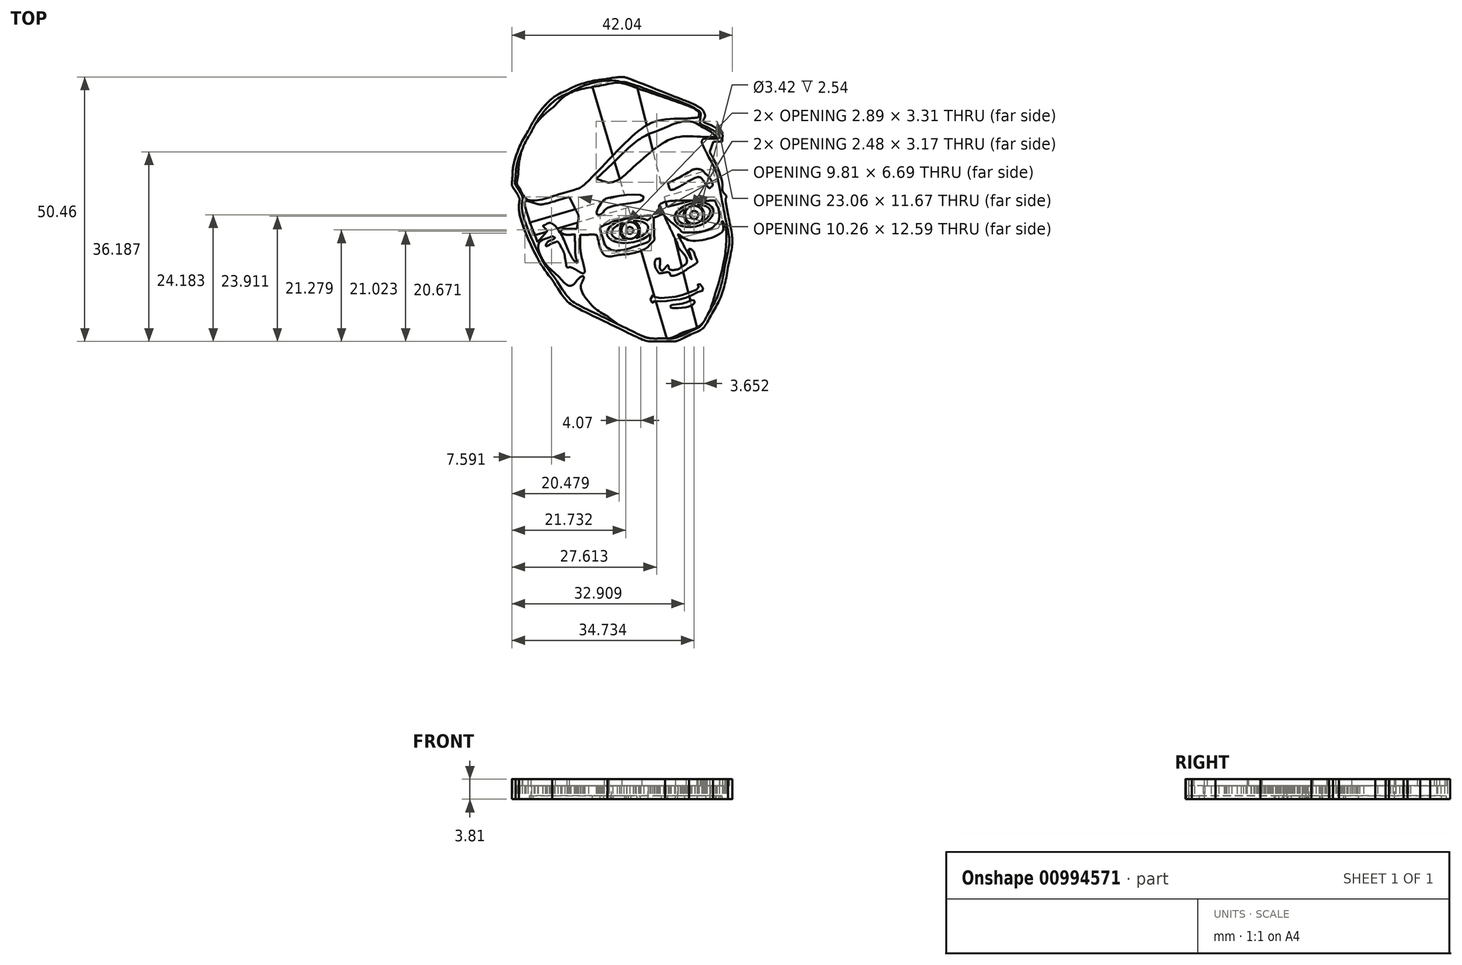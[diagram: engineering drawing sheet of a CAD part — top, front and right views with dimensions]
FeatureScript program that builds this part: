
annotation { "Feature Type Name" : "Feature", "Feature Type Description" : "" }
export const myFeature = defineFeature(function(context is Context, id is Id, definition is map)
    precondition{}
    {
        {
            var Q0;
            Q0=qCreatedBy(makeId("Top.planeOp"),FACE);
            var sketch = newSketch(context, id + "F0", { "sketchPlane" : qUnion([Q0])});
            skLineSegment(sketch, "E0", {"start": v(16.8, 11.07) * mm, "end": v(15.81, 13.05) * mm});
            skLineSegment(sketch, "E1", {"start": v(15.81, 13.05) * mm, "end": v(17.5, 13.05) * mm});
            skLineSegment(sketch, "E2", {"start": v(17.5, 14.49) * mm, "end": v(18.21, 13.92) * mm});
            skLineSegment(sketch, "E3", {"start": v(18.21, 13.92) * mm, "end": v(15.81, 13.9) * mm});
            skLineSegment(sketch, "E4", {"start": v(-3.94, 5.62) * mm, "end": v(-4.85, 5.88) * mm});
            skLineSegment(sketch, "E5", {"start": v(-4.85, 5.88) * mm, "end": v(-1.71, 8.87) * mm});
            skLineSegment(sketch, "E6", {"start": v(-8.35, -2.4) * mm, "end": v(-8.51, -3.6) * mm});
            skLineSegment(sketch, "E7", {"start": v(-8.51, -3.6) * mm, "end": v(-9.9, -3.6) * mm});
            skLineSegment(sketch, "E8", {"start": v(-15.1, -5.1) * mm, "end": v(-16.02, -6.17) * mm});
            skLineSegment(sketch, "E9", {"start": v(-16.02, -6.17) * mm, "end": v(-16.76, -4.25) * mm});
            skLineSegment(sketch, "E10", {"start": v(-12.13, 1.84) * mm, "end": v(-10.01, 2.46) * mm});
            skLineSegment(sketch, "E11", {"start": v(-10.01, 2.46) * mm, "end": v(-9.08, 0.63) * mm});
            skLineSegment(sketch, "E12", {"start": v(-7.9, -6.31) * mm, "end": v(-7.9, -4.73) * mm});
            skLineSegment(sketch, "E13", {"start": v(-7.9, -4.73) * mm, "end": v(-6.34, -4.73) * mm});
            skLineSegment(sketch, "E14", {"start": v(6.58, -16.66) * mm, "end": v(8.5, -16.78) * mm});
            skLineSegment(sketch, "E15", {"start": v(8.5, -16.78) * mm, "end": v(10.84, -16.48) * mm});
            skLineSegment(sketch, "E16", {"start": v(10.84, -16.48) * mm, "end": v(13.25, -15.7) * mm});
            skLineSegment(sketch, "E17", {"start": v(13.25, -15.7) * mm, "end": v(14.87, -14.91) * mm});
            skLineSegment(sketch, "E18", {"start": v(14.87, -14.91) * mm, "end": v(14.63, -14.37) * mm});
            skLineSegment(sketch, "E19", {"start": v(14.63, -14.37) * mm, "end": v(14.75, -14.01) * mm});
            skLineSegment(sketch, "E20", {"start": v(14.75, -14.01) * mm, "end": v(15.71, -14.61) * mm});
            skLineSegment(sketch, "E21", {"start": v(15.71, -14.61) * mm, "end": v(15.83, -15.4) * mm});
            skLineSegment(sketch, "E22", {"start": v(15.83, -15.4) * mm, "end": v(14.99, -15.58) * mm});
            skLineSegment(sketch, "E23", {"start": v(14.99, -15.58) * mm, "end": v(13.3, -16.42) * mm});
            skLineSegment(sketch, "E24", {"start": v(13.3, -16.42) * mm, "end": v(11.32, -17.08) * mm});
            skLineSegment(sketch, "E25", {"start": v(11.32, -17.08) * mm, "end": v(9.28, -17.26) * mm});
            skLineSegment(sketch, "E26", {"start": v(9.28, -17.26) * mm, "end": v(7.48, -17.44) * mm});
            skLineSegment(sketch, "E27", {"start": v(7.48, -17.44) * mm, "end": v(6.34, -17.44) * mm});
            skLineSegment(sketch, "E28", {"start": v(6.34, -17.44) * mm, "end": v(5.8, -17.74) * mm});
            skLineSegment(sketch, "E29", {"start": v(5.8, -17.74) * mm, "end": v(5.44, -16.96) * mm});
            skLineSegment(sketch, "E30", {"start": v(5.44, -16.96) * mm, "end": v(6.4, -16.24) * mm});
            skLineSegment(sketch, "E31", {"start": v(6.4, -16.24) * mm, "end": v(6.58, -16.66) * mm});
            skFitSpline(sketch, "E32", {"points": [v(-3.35, 24.9) * mm, v(-5.58, 24.59) * mm, v(-8.71, 23.66) * mm, v(-10.43, 22.78) * mm]});
            skFitSpline(sketch, "E33", {"points": [v(-10.43, 22.78) * mm, v(-12.83, 21.57) * mm, v(-16, 18.24) * mm, v(-17.86, 14.96) * mm]});
            skFitSpline(sketch, "E34", {"points": [v(-17.86, 14.96) * mm, v(-19.21, 12.62) * mm, v(-20.62, 8.56) * mm, v(-20.8, 6.55) * mm]});
            skFitSpline(sketch, "E35", {"points": [v(-20.8, 6.55) * mm, v(-20.93, 4.86) * mm, v(-20.88, 4.58) * mm, v(-20.2, 3.5) * mm]});
            skFitSpline(sketch, "E36", {"points": [v(-20.2, 3.5) * mm, v(-19.8, 2.86) * mm, v(-19.47, 2.1) * mm, v(-19.47, 1.81) * mm]});
            skFitSpline(sketch, "E37", {"points": [v(-19.47, 1.81) * mm, v(-19.47, -0.78) * mm, v(-15.85, -9.56) * mm, v(-13.23, -13.34) * mm]});
            skFitSpline(sketch, "E38", {"points": [v(-13.23, -13.34) * mm, v(-10.6, -17.18) * mm, v(-8.83, -18.53) * mm, v(-2.67, -21.55) * mm]});
            skFitSpline(sketch, "E39", {"points": [v(-2.67, -21.55) * mm, v(3.45, -24.52) * mm, v(5.09, -25.05) * mm, v(8.3, -25.05) * mm]});
            skFitSpline(sketch, "E40", {"points": [v(8.3, -25.05) * mm, v(10.34, -25.05) * mm, v(10.76, -24.94) * mm, v(12.85, -23.93) * mm]});
            skFitSpline(sketch, "E41", {"points": [v(12.85, -23.93) * mm, v(15.28, -22.77) * mm, v(15.87, -22.18) * mm, v(17.42, -19.4) * mm]});
            skFitSpline(sketch, "E42", {"points": [v(17.42, -19.4) * mm, v(18.66, -17.18) * mm, v(19.65, -14.27) * mm, v(20.3, -10.8) * mm]});
            skFitSpline(sketch, "E43", {"points": [v(20.3, -10.8) * mm, v(21.03, -7.05) * mm, v(21.03, -4.82) * mm, v(20.33, -1.1) * mm]});
            skFitSpline(sketch, "E44", {"points": [v(20.33, -1.1) * mm, v(20.02, 0.54) * mm, v(19.82, 2.04) * mm, v(19.9, 2.26) * mm]});
            skFitSpline(sketch, "E45", {"points": [v(19.9, 2.26) * mm, v(19.99, 2.46) * mm, v(19.85, 2.83) * mm, v(19.62, 3.06) * mm]});
            skFitSpline(sketch, "E46", {"points": [v(19.62, 3.06) * mm, v(19.4, 3.3) * mm, v(19.2, 3.82) * mm, v(19.2, 4.18) * mm]});
            skFitSpline(sketch, "E47", {"points": [v(19.2, 4.18) * mm, v(19.2, 5.2) * mm, v(17.96, 8.78) * mm, v(16.8, 11.07) * mm]});
            skFitSpline(sketch, "E48", {"points": [v(17.5, 13.05) * mm, v(19.11, 13.05) * mm, v(19.2, 13.07) * mm, v(19.2, 13.72) * mm]});
            skFitSpline(sketch, "E49", {"points": [v(19.2, 13.72) * mm, v(19.2, 14.43) * mm, v(17.76, 15.78) * mm, v(16.3, 16.46) * mm]});
            skFitSpline(sketch, "E50", {"points": [v(16.3, 16.46) * mm, v(15.76, 16.69) * mm, v(15.56, 16.97) * mm, v(15.67, 17.28) * mm]});
            skFitSpline(sketch, "E51", {"points": [v(15.67, 17.28) * mm, v(15.9, 17.98) * mm, v(15.36, 19.17) * mm, v(14.6, 19.68) * mm]});
            skFitSpline(sketch, "E52", {"points": [v(14.6, 19.68) * mm, v(14.2, 19.93) * mm, v(12.26, 20.78) * mm, v(10.28, 21.54) * mm]});
            skFitSpline(sketch, "E53", {"points": [v(10.28, 21.54) * mm, v(1.48, 25.01) * mm, v(0.1, 25.35) * mm, v(-3.35, 24.9) * mm]});
            skFitSpline(sketch, "E54", {"points": [v(3.68, 22.95) * mm, v(10.7, 20.55) * mm, v(14.68, 18.7) * mm, v(14.68, 17.82) * mm]});
            skFitSpline(sketch, "E55", {"points": [v(14.68, 17.82) * mm, v(14.68, 17.7) * mm, v(13.7, 17.53) * mm, v(12.51, 17.42) * mm]});
            skFitSpline(sketch, "E56", {"points": [v(12.51, 17.42) * mm, v(6.78, 16.97) * mm, v(2.72, 14.65) * mm, v(-3.8, 8.1) * mm]});
            skFitSpline(sketch, "E57", {"points": [v(-3.8, 8.1) * mm, v(-7.1, 4.8) * mm, v(-8.15, 4.13) * mm, v(-11.48, 3.14) * mm]});
            skFitSpline(sketch, "E58", {"points": [v(-11.48, 3.14) * mm, v(-15.85, 1.87) * mm, v(-18.22, 2.12) * mm, v(-19.4, 4.07) * mm]});
            skFitSpline(sketch, "E59", {"points": [v(-19.4, 4.07) * mm, v(-19.94, 4.92) * mm, v(-19.97, 5.23) * mm, v(-19.75, 6.7) * mm]});
            skFitSpline(sketch, "E60", {"points": [v(-19.75, 6.7) * mm, v(-19.1, 11.15) * mm, v(-16.25, 16.57) * mm, v(-12.92, 19.7) * mm]});
            skFitSpline(sketch, "E61", {"points": [v(-12.92, 19.7) * mm, v(-10.72, 21.8) * mm, v(-8.35, 22.87) * mm, v(-4.37, 23.63) * mm]});
            skFitSpline(sketch, "E62", {"points": [v(-4.37, 23.63) * mm, v(-1.04, 24.25) * mm, v(0.15, 24.17) * mm, v(3.68, 22.95) * mm]});
            skFitSpline(sketch, "E63", {"points": [v(15.47, 15.76) * mm, v(16.2, 15.39) * mm, v(17.11, 14.82) * mm, v(17.5, 14.49) * mm]});
            skFitSpline(sketch, "E64", {"points": [v(15.81, 13.9) * mm, v(10.73, 13.9) * mm, v(7.18, 12.28) * mm, v(1.53, 7.51) * mm]});
            skFitSpline(sketch, "E65", {"points": [v(1.53, 7.51) * mm, v(-0.42, 5.88) * mm, v(-2.33, 5.23) * mm, v(-3.94, 5.62) * mm]});
            skFitSpline(sketch, "E66", {"points": [v(-1.71, 8.87) * mm, v(1.65, 12.11) * mm, v(4.35, 14.06) * mm, v(6.78, 15.05) * mm]});
            skFitSpline(sketch, "E67", {"points": [v(6.78, 15.05) * mm, v(10.73, 16.63) * mm, v(13.33, 16.83) * mm, v(15.47, 15.76) * mm]});
            skFitSpline(sketch, "E68", {"points": [v(15.33, 11.72) * mm, v(16.4, 9.57) * mm, v(18.63, 3.08) * mm, v(18.63, 2.12) * mm]});
            skFitSpline(sketch, "E69", {"points": [v(18.63, 2.12) * mm, v(18.63, 2.1) * mm, v(18.27, 2.26) * mm, v(17.82, 2.55) * mm]});
            skFitSpline(sketch, "E70", {"points": [v(17.82, 2.55) * mm, v(17.08, 2.94) * mm, v(16.77, 2.97) * mm, v(15.2, 2.66) * mm]});
            skFitSpline(sketch, "E71", {"points": [v(15.2, 2.66) * mm, v(12.4, 2.1) * mm, v(9.89, 1.2) * mm, v(9.52, 0.6) * mm]});
            skFitSpline(sketch, "E72", {"points": [v(9.52, 0.6) * mm, v(9.32, 0.26) * mm, v(8.87, 0.06) * mm, v(8.33, 0.06) * mm]});
            skFitSpline(sketch, "E73", {"points": [v(8.33, 0.06) * mm, v(7.88, 0.06) * mm, v(7.04, -0.08) * mm, v(6.44, -0.22) * mm]});
            skFitSpline(sketch, "E74", {"points": [v(6.44, -0.22) * mm, v(5.88, -0.39) * mm, v(4.3, -0.56) * mm, v(2.92, -0.61) * mm]});
            skFitSpline(sketch, "E75", {"points": [v(2.92, -0.61) * mm, v(-0.95, -0.78) * mm, v(-4.79, -2.22) * mm, v(-4.79, -3.52) * mm]});
            skFitSpline(sketch, "E76", {"points": [v(-4.79, -3.52) * mm, v(-4.79, -3.75) * mm, v(-5.13, -3.89) * mm, v(-5.75, -3.89) * mm]});
            skFitSpline(sketch, "E77", {"points": [v(-5.75, -3.89) * mm, v(-7.41, -3.89) * mm, v(-7.56, -3.72) * mm, v(-7.27, -2.4) * mm]});
            skFitSpline(sketch, "E78", {"points": [v(-7.27, -2.4) * mm, v(-7.05, -1.3) * mm, v(-7.13, -1) * mm, v(-8.04, 0.77) * mm]});
            skFitSpline(sketch, "E79", {"points": [v(-8.04, 0.77) * mm, v(-8.8, 2.2) * mm, v(-8.97, 2.77) * mm, v(-8.68, 2.86) * mm]});
            skFitSpline(sketch, "E80", {"points": [v(-8.68, 2.86) * mm, v(-8.49, 2.91) * mm, v(-7.75, 3.37) * mm, v(-7.05, 3.85) * mm]});
            skFitSpline(sketch, "E81", {"points": [v(-7.05, 3.85) * mm, v(-5.86, 4.64) * mm, v(-5.6, 4.7) * mm, v(-3.2, 4.72) * mm]});
            skFitSpline(sketch, "E82", {"points": [v(-3.2, 4.72) * mm, v(-0.3, 4.72) * mm, v(-0.3, 4.72) * mm, v(3.82, 8.1) * mm]});
            skFitSpline(sketch, "E83", {"points": [v(3.82, 8.1) * mm, v(6.44, 10.28) * mm, v(9.15, 11.7) * mm, v(12.14, 12.45) * mm]});
            skFitSpline(sketch, "E84", {"points": [v(12.14, 12.45) * mm, v(13.3, 12.76) * mm, v(14.35, 13.02) * mm, v(14.46, 13.02) * mm]});
            skFitSpline(sketch, "E85", {"points": [v(14.46, 13.02) * mm, v(14.57, 13.05) * mm, v(14.97, 12.45) * mm, v(15.33, 11.72) * mm]});
            skFitSpline(sketch, "E86", {"points": [v(-9.9, -3.6) * mm, v(-10.63, -3.6) * mm, v(-11.3, -3.72) * mm, v(-11.42, -3.86) * mm]});
            skFitSpline(sketch, "E87", {"points": [v(-11.42, -3.86) * mm, v(-11.65, -4.25) * mm, v(-10.63, -4.73) * mm, v(-9.67, -4.73) * mm]});
            skFitSpline(sketch, "E88", {"points": [v(-9.67, -4.73) * mm, v(-8.88, -4.73) * mm, v(-8.88, -4.76) * mm, v(-8.88, -6.48) * mm]});
            skFitSpline(sketch, "E89", {"points": [v(-8.88, -6.48) * mm, v(-8.88, -7.47) * mm, v(-8.8, -8.69) * mm, v(-8.68, -9.22) * mm]});
            skFitSpline(sketch, "E90", {"points": [v(-8.68, -9.22) * mm, v(-8.49, -10.07) * mm, v(-8.51, -10.12) * mm, v(-8.94, -9.79) * mm]});
            skFitSpline(sketch, "E91", {"points": [v(-8.94, -9.79) * mm, v(-9.2, -9.56) * mm, v(-9.78, -8.57) * mm, v(-10.24, -7.58) * mm]});
            skFitSpline(sketch, "E92", {"points": [v(-10.24, -7.58) * mm, v(-11.56, -4.62) * mm, v(-13.54, -2.48) * mm, v(-14.58, -2.87) * mm]});
            skFitSpline(sketch, "E93", {"points": [v(-14.58, -2.87) * mm, v(-14.98, -3.04) * mm, v(-14.98, -3.1) * mm, v(-14.58, -3.55) * mm]});
            skFitSpline(sketch, "E94", {"points": [v(-14.58, -3.55) * mm, v(-14.19, -4) * mm, v(-14.24, -4.11) * mm, v(-15.1, -5.1) * mm]});
            skFitSpline(sketch, "E95", {"points": [v(-16.76, -4.25) * mm, v(-17.57, -2.1) * mm, v(-18.48, 1.42) * mm, v(-18.28, 1.62) * mm]});
            skFitSpline(sketch, "E96", {"points": [v(-18.28, 1.62) * mm, v(-18.22, 1.7) * mm, v(-17.72, 1.62) * mm, v(-17.18, 1.47) * mm]});
            skFitSpline(sketch, "E97", {"points": [v(-17.18, 1.47) * mm, v(-15.77, 1.05) * mm, v(-14.5, 1.16) * mm, v(-12.13, 1.84) * mm]});
            skFitSpline(sketch, "E98", {"points": [v(-9.08, 0.63) * mm, v(-8.32, -0.9) * mm, v(-8.2, -1.4) * mm, v(-8.35, -2.4) * mm]});
            skFitSpline(sketch, "E99", {"points": [v(18.07, 1.02) * mm, v(18.55, -0.2) * mm, v(18.4, -2.34) * mm, v(17.87, -2.82) * mm]});
            skFitSpline(sketch, "E100", {"points": [v(17.87, -2.82) * mm, v(17.08, -3.52) * mm, v(14.68, -4.23) * mm, v(13.05, -4.28) * mm]});
            skFitSpline(sketch, "E101", {"points": [v(13.05, -4.28) * mm, v(11.83, -4.31) * mm, v(11.47, -4.2) * mm, v(11.13, -3.77) * mm]});
            skFitSpline(sketch, "E102", {"points": [v(11.13, -3.77) * mm, v(7.36, 1.09) * mm, v(15.3, 1.7) * mm, v(16.04, 1.73) * mm]});
            skFitSpline(sketch, "E103", {"points": [v(16.04, 1.73) * mm, v(17.68, 1.76) * mm, v(17.82, 1.7) * mm, v(18.07, 1.02) * mm]});
            skFitSpline(sketch, "E104", {"points": [v(9.4, -3.86) * mm, v(10.14, -5.38) * mm, v(10.73, -6.74) * mm, v(10.73, -6.85) * mm]});
            skFitSpline(sketch, "E105", {"points": [v(10.73, -6.85) * mm, v(10.73, -6.94) * mm, v(11.04, -7.44) * mm, v(11.44, -7.95) * mm]});
            skFitSpline(sketch, "E106", {"points": [v(11.44, -7.95) * mm, v(12.31, -9.1) * mm, v(12.34, -10.2) * mm, v(11.52, -10.77) * mm]});
            skFitSpline(sketch, "E107", {"points": [v(11.52, -10.77) * mm, v(10.76, -11.31) * mm, v(9.15, -11.37) * mm, v(8.95, -10.86) * mm]});
            skFitSpline(sketch, "E108", {"points": [v(8.95, -10.86) * mm, v(8.84, -10.58) * mm, v(8.76, -10.58) * mm, v(8.45, -10.86) * mm]});
            skFitSpline(sketch, "E109", {"points": [v(8.45, -10.86) * mm, v(7.77, -11.54) * mm, v(7.35, -11.28) * mm, v(7.35, -10.2) * mm]});
            skFitSpline(sketch, "E110", {"points": [v(7.35, -10.2) * mm, v(7.35, -9.53) * mm, v(7.23, -9.25) * mm, v(7, -9.3) * mm]});
            skFitSpline(sketch, "E111", {"points": [v(7, -9.3) * mm, v(6.5, -9.48) * mm, v(6.39, -10.77) * mm, v(6.78, -11.54) * mm]});
            skFitSpline(sketch, "E112", {"points": [v(6.78, -11.54) * mm, v(7.06, -12.02) * mm, v(7.29, -12.1) * mm, v(8.08, -11.99) * mm]});
            skFitSpline(sketch, "E113", {"points": [v(8.08, -11.99) * mm, v(8.59, -11.9) * mm, v(9.1, -11.96) * mm, v(9.2, -12.1) * mm]});
            skFitSpline(sketch, "E114", {"points": [v(9.2, -12.1) * mm, v(9.46, -12.55) * mm, v(11.3, -12.04) * mm, v(12.68, -11.17) * mm]});
            skFitSpline(sketch, "E115", {"points": [v(12.68, -11.17) * mm, v(14.29, -10.15) * mm, v(14.43, -9.87) * mm, v(13.98, -8.74) * mm]});
            skFitSpline(sketch, "E116", {"points": [v(13.98, -8.74) * mm, v(13.53, -7.73) * mm, v(12.82, -7.47) * mm, v(13.08, -8.43) * mm]});
            skFitSpline(sketch, "E117", {"points": [v(13.08, -8.43) * mm, v(13.33, -9.45) * mm, v(12.96, -8.88) * mm, v(11.5, -6.15) * mm]});
            skFitSpline(sketch, "E118", {"points": [v(11.5, -6.15) * mm, v(10.82, -4.9) * mm, v(10.76, -4.68) * mm, v(11.21, -4.88) * mm]});
            skFitSpline(sketch, "E119", {"points": [v(11.21, -4.88) * mm, v(13.5, -5.9) * mm, v(19.14, -4.23) * mm, v(19.23, -2.53) * mm]});
            skFitSpline(sketch, "E120", {"points": [v(19.23, -2.53) * mm, v(19.23, -2.14) * mm, v(19.28, -2.17) * mm, v(19.48, -2.62) * mm]});
            skFitSpline(sketch, "E121", {"points": [v(19.48, -2.62) * mm, v(19.88, -3.55) * mm, v(19.8, -8.1) * mm, v(19.34, -10.5) * mm]});
            skFitSpline(sketch, "E122", {"points": [v(19.34, -10.5) * mm, v(19.11, -11.7) * mm, v(18.52, -13.85) * mm, v(18.04, -15.29) * mm]});
            skFitSpline(sketch, "E123", {"points": [v(18.04, -15.29) * mm, v(16.46, -20.03) * mm, v(14.74, -22.2) * mm, v(11.7, -23.36) * mm]});
            skFitSpline(sketch, "E124", {"points": [v(11.7, -23.36) * mm, v(8, -24.74) * mm, v(1.98, -23.45) * mm, v(-2.84, -20.2) * mm]});
            skFitSpline(sketch, "E125", {"points": [v(-2.84, -20.2) * mm, v(-5.3, -18.6) * mm, v(-7.78, -15) * mm, v(-7.44, -13.62) * mm]});
            skFitSpline(sketch, "E126", {"points": [v(-7.44, -13.62) * mm, v(-7.22, -12.75) * mm, v(-7.67, -12.7) * mm, v(-8.51, -13.48) * mm]});
            skFitSpline(sketch, "E127", {"points": [v(-8.51, -13.48) * mm, v(-9.59, -14.47) * mm, v(-10.58, -14.22) * mm, v(-12.16, -12.55) * mm]});
            skFitSpline(sketch, "E128", {"points": [v(-12.16, -12.55) * mm, v(-15.03, -9.56) * mm, v(-15.77, -6.34) * mm, v(-13.82, -5.3) * mm]});
            skFitSpline(sketch, "E129", {"points": [v(-13.82, -5.3) * mm, v(-13.51, -5.13) * mm, v(-13.12, -5.07) * mm, v(-12.92, -5.19) * mm]});
            skFitSpline(sketch, "E130", {"points": [v(-12.92, -5.19) * mm, v(-12.72, -5.3) * mm, v(-12.89, -5.52) * mm, v(-13.37, -5.78) * mm]});
            skFitSpline(sketch, "E131", {"points": [v(-13.37, -5.78) * mm, v(-14.19, -6.2) * mm, v(-14.41, -6.9) * mm, v(-13.6, -6.57) * mm]});
            skFitSpline(sketch, "E132", {"points": [v(-13.6, -6.57) * mm, v(-12.35, -6.06) * mm, v(-12.16, -6.09) * mm, v(-11.6, -7.02) * mm]});
            skFitSpline(sketch, "E133", {"points": [v(-11.6, -7.02) * mm, v(-11.25, -7.56) * mm, v(-10.91, -8.43) * mm, v(-10.83, -8.97) * mm]});
            skFitSpline(sketch, "E134", {"points": [v(-10.83, -8.97) * mm, v(-10.55, -10.6) * mm, v(-10.4, -10.94) * mm, v(-9.98, -10.94) * mm]});
            skFitSpline(sketch, "E135", {"points": [v(-9.98, -10.94) * mm, v(-9.76, -10.94) * mm, v(-9.05, -11.23) * mm, v(-8.46, -11.56) * mm]});
            skFitSpline(sketch, "E136", {"points": [v(-8.46, -11.56) * mm, v(-7.87, -11.93) * mm, v(-7.27, -12.1) * mm, v(-7.16, -11.99) * mm]});
            skFitSpline(sketch, "E137", {"points": [v(-7.16, -11.99) * mm, v(-7.05, -11.87) * mm, v(-7.16, -10.91) * mm, v(-7.41, -9.84) * mm]});
            skFitSpline(sketch, "E138", {"points": [v(-7.41, -9.84) * mm, v(-7.7, -8.77) * mm, v(-7.9, -7.19) * mm, v(-7.9, -6.31) * mm]});
            skFitSpline(sketch, "E139", {"points": [v(-6.34, -4.73) * mm, v(-5.1, -4.73) * mm, v(-4.73, -4.85) * mm, v(-4.62, -5.21) * mm]});
            skFitSpline(sketch, "E140", {"points": [v(-4.62, -5.21) * mm, v(-3.72, -8.1) * mm, v(-2.76, -8.85) * mm, v(-0.39, -8.57) * mm]});
            skFitSpline(sketch, "E141", {"points": [v(-0.39, -8.57) * mm, v(1.93, -8.32) * mm, v(4.66, -7.36) * mm, v(5.48, -6.51) * mm]});
            skFitSpline(sketch, "E142", {"points": [v(5.48, -6.51) * mm, v(6.22, -5.78) * mm, v(6.25, -5.6) * mm, v(6.16, -3.63) * mm]});
            skFitSpline(sketch, "E143", {"points": [v(6.16, -3.63) * mm, v(6.1, -1.77) * mm, v(6.13, -1.52) * mm, v(6.64, -1.32) * mm]});
            skFitSpline(sketch, "E144", {"points": [v(6.64, -1.32) * mm, v(7.88, -0.84) * mm, v(8.08, -1.04) * mm, v(9.4, -3.86) * mm]});
            skFitSpline(sketch, "E145", {"points": [v(5.03, -1.91) * mm, v(5.36, -3.9) * mm, v(5.36, -3.96) * mm, v(5.37, -4.82) * mm]});
            skFitSpline(sketch, "E146", {"points": [v(5.37, -4.82) * mm, v(5.37, -5.75) * mm, v(4.66, -6.29) * mm, v(2.58, -6.96) * mm]});
            skFitSpline(sketch, "E147", {"points": [v(2.58, -6.96) * mm, v(0.63, -7.58) * mm, v(-1.66, -7.73) * mm, v(-2.53, -7.27) * mm]});
            skFitSpline(sketch, "E148", {"points": [v(-2.53, -7.27) * mm, v(-2.84, -7.1) * mm, v(-3.3, -6.29) * mm, v(-3.55, -5.44) * mm]});
            skFitSpline(sketch, "E149", {"points": [v(-3.55, -5.44) * mm, v(-4.11, -3.7) * mm, v(-3.91, -3.24) * mm, v(-2.4, -2.59) * mm]});
            skFitSpline(sketch, "E150", {"points": [v(-2.4, -2.59) * mm, v(-1.23, -2.08) * mm, v(5.77, -1.15) * mm, v(5.03, -1.91) * mm]});
            skFitSpline(sketch, "E151", {"points": [v(9.5, -18.25) * mm, v(9.7, -18.25) * mm, v(9.9, -18.25) * mm, v(10.1, -18.25) * mm]});
            skFitSpline(sketch, "E152", {"points": [v(10.1, -18.25) * mm, v(10.14, -18.25) * mm, v(10.2, -18.25) * mm, v(10.24, -18.25) * mm]});
            skFitSpline(sketch, "E153", {"points": [v(10.24, -18.25) * mm, v(10.25, -18.25) * mm, v(10.26, -18.25) * mm, v(10.27, -18.25) * mm]});
            skFitSpline(sketch, "E154", {"points": [v(10.27, -18.25) * mm, v(10.28, -18.25) * mm, v(10.3, -18.25) * mm, v(10.3, -18.25) * mm]});
            skFitSpline(sketch, "E155", {"points": [v(10.3, -18.25) * mm, v(10.31, -18.24) * mm, v(10.32, -18.22) * mm, v(10.33, -18.22) * mm]});
            skFitSpline(sketch, "E156", {"points": [v(10.33, -18.22) * mm, v(10.34, -18.21) * mm, v(10.35, -18.22) * mm, v(10.36, -18.22) * mm]});
            skFitSpline(sketch, "E157", {"points": [v(10.36, -18.22) * mm, v(10.37, -18.22) * mm, v(10.38, -18.22) * mm, v(10.4, -18.22) * mm]});
            skFitSpline(sketch, "E158", {"points": [v(10.4, -18.22) * mm, v(10.46, -18.22) * mm, v(10.53, -18.22) * mm, v(10.6, -18.22) * mm]});
            skFitSpline(sketch, "E159", {"points": [v(10.6, -18.22) * mm, v(10.62, -18.22) * mm, v(10.68, -18.22) * mm, v(10.7, -18.22) * mm]});
            skFitSpline(sketch, "E160", {"points": [v(10.7, -18.22) * mm, v(10.7, -18.2) * mm, v(10.7, -18.2) * mm, v(10.72, -18.19) * mm]});
            skFitSpline(sketch, "E161", {"points": [v(10.72, -18.19) * mm, v(10.74, -18.18) * mm, v(10.82, -18.2) * mm, v(10.84, -18.19) * mm]});
            skFitSpline(sketch, "E162", {"points": [v(10.84, -18.19) * mm, v(10.86, -18.18) * mm, v(10.86, -18.16) * mm, v(10.87, -18.16) * mm]});
            skFitSpline(sketch, "E163", {"points": [v(10.87, -18.16) * mm, v(10.88, -18.15) * mm, v(10.9, -18.16) * mm, v(10.9, -18.16) * mm]});
            skFitSpline(sketch, "E164", {"points": [v(10.9, -18.16) * mm, v(10.92, -18.15) * mm, v(10.92, -18.13) * mm, v(10.93, -18.13) * mm]});
            skFitSpline(sketch, "E165", {"points": [v(10.93, -18.13) * mm, v(10.95, -18.12) * mm, v(10.98, -18.13) * mm, v(11, -18.13) * mm]});
            skFitSpline(sketch, "E166", {"points": [v(11, -18.13) * mm, v(11, -18.12) * mm, v(11.01, -18.1) * mm, v(11.02, -18.1) * mm]});
            skFitSpline(sketch, "E167", {"points": [v(11.02, -18.1) * mm, v(11.03, -18.09) * mm, v(11.1, -18.1) * mm, v(11.11, -18.1) * mm]});
            skFitSpline(sketch, "E168", {"points": [v(11.11, -18.1) * mm, v(11.12, -18.09) * mm, v(11.1, -18.07) * mm, v(11.11, -18.06) * mm]});
            skFitSpline(sketch, "E169", {"points": [v(11.11, -18.06) * mm, v(11.12, -18.06) * mm, v(11.14, -18.07) * mm, v(11.14, -18.06) * mm]});
            skFitSpline(sketch, "E170", {"points": [v(11.14, -18.06) * mm, v(11.15, -18.06) * mm, v(11.14, -18.04) * mm, v(11.14, -18.03) * mm]});
            skFitSpline(sketch, "E171", {"points": [v(11.14, -18.03) * mm, v(11.16, -18.01) * mm, v(11.2, -18.07) * mm, v(11.23, -18) * mm]});
            skFitSpline(sketch, "E172", {"points": [v(11.23, -18) * mm, v(11.24, -18) * mm, v(11.23, -17.98) * mm, v(11.23, -17.97) * mm]});
            skFitSpline(sketch, "E173", {"points": [v(11.23, -17.97) * mm, v(11.24, -17.96) * mm, v(11.33, -17.98) * mm, v(11.35, -17.97) * mm]});
            skFitSpline(sketch, "E174", {"points": [v(11.35, -17.97) * mm, v(11.36, -17.97) * mm, v(11.35, -17.95) * mm, v(11.35, -17.94) * mm]});
            skFitSpline(sketch, "E175", {"points": [v(11.35, -17.94) * mm, v(11.36, -17.94) * mm, v(11.37, -17.95) * mm, v(11.38, -17.94) * mm]});
            skFitSpline(sketch, "E176", {"points": [v(11.38, -17.94) * mm, v(11.4, -17.94) * mm, v(11.42, -17.92) * mm, v(11.44, -17.91) * mm]});
            skFitSpline(sketch, "E177", {"points": [v(11.44, -17.91) * mm, v(11.46, -17.9) * mm, v(11.52, -17.92) * mm, v(11.53, -17.91) * mm]});
            skFitSpline(sketch, "E178", {"points": [v(11.53, -17.91) * mm, v(11.55, -17.9) * mm, v(11.55, -17.9) * mm, v(11.56, -17.88) * mm]});
            skFitSpline(sketch, "E179", {"points": [v(11.56, -17.88) * mm, v(11.58, -17.88) * mm, v(11.65, -17.9) * mm, v(11.65, -17.88) * mm]});
            skFitSpline(sketch, "E180", {"points": [v(11.65, -17.88) * mm, v(11.66, -17.88) * mm, v(11.65, -17.86) * mm, v(11.65, -17.85) * mm]});
            skFitSpline(sketch, "E181", {"points": [v(11.65, -17.85) * mm, v(11.66, -17.85) * mm, v(11.68, -17.86) * mm, v(11.68, -17.85) * mm]});
            skFitSpline(sketch, "E182", {"points": [v(11.68, -17.85) * mm, v(11.7, -17.85) * mm, v(11.7, -17.83) * mm, v(11.71, -17.82) * mm]});
            skFitSpline(sketch, "E183", {"points": [v(11.71, -17.82) * mm, v(11.73, -17.82) * mm, v(11.85, -17.83) * mm, v(11.86, -17.82) * mm]});
            skFitSpline(sketch, "E184", {"points": [v(11.86, -17.82) * mm, v(11.88, -17.82) * mm, v(11.88, -17.8) * mm, v(11.9, -17.8) * mm]});
            skFitSpline(sketch, "E185", {"points": [v(11.9, -17.8) * mm, v(11.9, -17.8) * mm, v(11.97, -17.8) * mm, v(11.98, -17.8) * mm]});
            skFitSpline(sketch, "E186", {"points": [v(11.98, -17.8) * mm, v(12.04, -17.8) * mm, v(12.1, -17.8) * mm, v(12.16, -17.8) * mm]});
            skFitSpline(sketch, "E187", {"points": [v(12.16, -17.8) * mm, v(12.18, -17.8) * mm, v(12.28, -17.8) * mm, v(12.28, -17.8) * mm]});
            skFitSpline(sketch, "E188", {"points": [v(12.28, -17.8) * mm, v(12.3, -17.79) * mm, v(12.28, -17.77) * mm, v(12.28, -17.76) * mm]});
            skFitSpline(sketch, "E189", {"points": [v(12.28, -17.76) * mm, v(12.3, -17.75) * mm, v(12.33, -17.78) * mm, v(12.34, -17.76) * mm]});
            skFitSpline(sketch, "E190", {"points": [v(12.34, -17.76) * mm, v(12.35, -17.76) * mm, v(12.34, -17.74) * mm, v(12.34, -17.73) * mm]});
            skFitSpline(sketch, "E191", {"points": [v(12.34, -17.73) * mm, v(12.35, -17.73) * mm, v(12.37, -17.74) * mm, v(12.38, -17.73) * mm]});
            skFitSpline(sketch, "E192", {"points": [v(12.38, -17.73) * mm, v(12.41, -17.72) * mm, v(12.46, -17.69) * mm, v(12.5, -17.67) * mm]});
            skFitSpline(sketch, "E193", {"points": [v(12.5, -17.67) * mm, v(12.5, -17.67) * mm, v(12.52, -17.68) * mm, v(12.53, -17.67) * mm]});
            skFitSpline(sketch, "E194", {"points": [v(12.53, -17.67) * mm, v(12.54, -17.67) * mm, v(12.54, -17.65) * mm, v(12.56, -17.64) * mm]});
            skFitSpline(sketch, "E195", {"points": [v(12.56, -17.64) * mm, v(12.56, -17.64) * mm, v(12.58, -17.65) * mm, v(12.59, -17.64) * mm]});
            skFitSpline(sketch, "E196", {"points": [v(12.59, -17.64) * mm, v(12.6, -17.64) * mm, v(12.6, -17.62) * mm, v(12.62, -17.61) * mm]});
            skFitSpline(sketch, "E197", {"points": [v(12.62, -17.61) * mm, v(12.63, -17.6) * mm, v(12.7, -17.62) * mm, v(12.7, -17.61) * mm]});
            skFitSpline(sketch, "E198", {"points": [v(12.7, -17.61) * mm, v(12.71, -17.6) * mm, v(12.7, -17.6) * mm, v(12.7, -17.58) * mm]});
            skFitSpline(sketch, "E199", {"points": [v(12.7, -17.58) * mm, v(12.71, -17.58) * mm, v(12.78, -17.6) * mm, v(12.8, -17.58) * mm]});
            skFitSpline(sketch, "E200", {"points": [v(12.8, -17.58) * mm, v(12.8, -17.58) * mm, v(12.81, -17.56) * mm, v(12.83, -17.55) * mm]});
            skFitSpline(sketch, "E201", {"points": [v(12.83, -17.55) * mm, v(12.83, -17.55) * mm, v(12.85, -17.56) * mm, v(12.86, -17.55) * mm]});
            skFitSpline(sketch, "E202", {"points": [v(12.86, -17.55) * mm, v(12.86, -17.55) * mm, v(12.85, -17.53) * mm, v(12.86, -17.52) * mm]});
            skFitSpline(sketch, "E203", {"points": [v(12.86, -17.52) * mm, v(12.86, -17.52) * mm, v(12.88, -17.52) * mm, v(12.89, -17.52) * mm]});
            skFitSpline(sketch, "E204", {"points": [v(12.89, -17.52) * mm, v(12.9, -17.52) * mm, v(12.93, -17.53) * mm, v(12.95, -17.52) * mm]});
            skFitSpline(sketch, "E205", {"points": [v(12.95, -17.52) * mm, v(12.95, -17.52) * mm, v(12.94, -17.5) * mm, v(12.95, -17.5) * mm]});
            skFitSpline(sketch, "E206", {"points": [v(12.95, -17.5) * mm, v(12.96, -17.48) * mm, v(13.02, -17.5) * mm, v(13.04, -17.5) * mm]});
            skFitSpline(sketch, "E207", {"points": [v(13.04, -17.5) * mm, v(13.04, -17.49) * mm, v(13.03, -17.47) * mm, v(13.04, -17.46) * mm]});
            skFitSpline(sketch, "E208", {"points": [v(13.04, -17.46) * mm, v(13.05, -17.45) * mm, v(13.08, -17.47) * mm, v(13.1, -17.46) * mm]});
            skFitSpline(sketch, "E209", {"points": [v(13.1, -17.46) * mm, v(13.1, -17.46) * mm, v(13.11, -17.44) * mm, v(13.13, -17.43) * mm]});
            skFitSpline(sketch, "E210", {"points": [v(13.13, -17.43) * mm, v(13.14, -17.43) * mm, v(13.15, -17.44) * mm, v(13.16, -17.43) * mm]});
            skFitSpline(sketch, "E211", {"points": [v(13.16, -17.43) * mm, v(13.16, -17.43) * mm, v(13.15, -17.41) * mm, v(13.16, -17.4) * mm]});
            skFitSpline(sketch, "E212", {"points": [v(13.16, -17.4) * mm, v(13.17, -17.39) * mm, v(13.2, -17.41) * mm, v(13.22, -17.4) * mm]});
            skFitSpline(sketch, "E213", {"points": [v(13.22, -17.4) * mm, v(13.24, -17.4) * mm, v(13.26, -17.38) * mm, v(13.28, -17.37) * mm]});
            skFitSpline(sketch, "E214", {"points": [v(13.28, -17.37) * mm, v(13.29, -17.37) * mm, v(13.36, -17.38) * mm, v(13.37, -17.37) * mm]});
            skFitSpline(sketch, "E215", {"points": [v(13.37, -17.37) * mm, v(13.37, -17.37) * mm, v(13.36, -17.35) * mm, v(13.37, -17.34) * mm]});
            skFitSpline(sketch, "E216", {"points": [v(13.37, -17.34) * mm, v(13.38, -17.33) * mm, v(13.4, -17.35) * mm, v(13.43, -17.34) * mm]});
            skFitSpline(sketch, "E217", {"points": [v(13.43, -17.34) * mm, v(13.44, -17.34) * mm, v(13.44, -17.32) * mm, v(13.46, -17.31) * mm]});
            skFitSpline(sketch, "E218", {"points": [v(13.46, -17.31) * mm, v(13.46, -17.3) * mm, v(13.56, -17.31) * mm, v(13.58, -17.31) * mm]});
            skFitSpline(sketch, "E219", {"points": [v(13.58, -17.31) * mm, v(13.6, -17.31) * mm, v(13.62, -17.31) * mm, v(13.64, -17.31) * mm]});
            skFitSpline(sketch, "E220", {"points": [v(13.64, -17.31) * mm, v(13.65, -17.31) * mm, v(13.67, -17.3) * mm, v(13.67, -17.31) * mm]});
            skFitSpline(sketch, "E221", {"points": [v(13.67, -17.31) * mm, v(13.67, -17.36) * mm, v(13.53, -17.23) * mm, v(13.7, -17.31) * mm]});
            skFitSpline(sketch, "E222", {"points": [v(13.7, -17.31) * mm, v(13.7, -17.32) * mm, v(13.69, -17.34) * mm, v(13.7, -17.34) * mm]});
            skFitSpline(sketch, "E223", {"points": [v(13.7, -17.34) * mm, v(13.71, -17.35) * mm, v(13.74, -17.34) * mm, v(13.76, -17.34) * mm]});
            skFitSpline(sketch, "E224", {"points": [v(13.76, -17.34) * mm, v(13.78, -17.35) * mm, v(13.8, -17.4) * mm, v(13.82, -17.4) * mm]});
            skFitSpline(sketch, "E225", {"points": [v(13.82, -17.4) * mm, v(13.83, -17.4) * mm, v(13.84, -17.4) * mm, v(13.85, -17.4) * mm]});
            skFitSpline(sketch, "E226", {"points": [v(13.85, -17.4) * mm, v(13.85, -17.41) * mm, v(13.85, -17.42) * mm, v(13.85, -17.43) * mm]});
            skFitSpline(sketch, "E227", {"points": [v(13.85, -17.43) * mm, v(13.85, -17.48) * mm, v(13.85, -17.53) * mm, v(13.85, -17.58) * mm]});
            skFitSpline(sketch, "E228", {"points": [v(13.85, -17.58) * mm, v(13.85, -17.64) * mm, v(13.85, -17.7) * mm, v(13.85, -17.76) * mm]});
            skFitSpline(sketch, "E229", {"points": [v(13.85, -17.76) * mm, v(13.85, -17.77) * mm, v(13.86, -17.8) * mm, v(13.85, -17.8) * mm]});
            skFitSpline(sketch, "E230", {"points": [v(13.85, -17.8) * mm, v(13.84, -17.8) * mm, v(13.85, -17.75) * mm, v(13.85, -17.76) * mm]});
            skFitSpline(sketch, "E231", {"points": [v(13.85, -17.76) * mm, v(13.85, -17.78) * mm, v(13.85, -17.8) * mm, v(13.85, -17.82) * mm]});
            skFitSpline(sketch, "E232", {"points": [v(13.85, -17.82) * mm, v(13.84, -17.84) * mm, v(13.82, -17.84) * mm, v(13.82, -17.85) * mm]});
            skFitSpline(sketch, "E233", {"points": [v(13.82, -17.85) * mm, v(13.81, -17.86) * mm, v(13.82, -17.88) * mm, v(13.82, -17.88) * mm]});
            skFitSpline(sketch, "E234", {"points": [v(13.82, -17.88) * mm, v(13.81, -17.9) * mm, v(13.8, -17.88) * mm, v(13.79, -17.88) * mm]});
            skFitSpline(sketch, "E235", {"points": [v(13.79, -17.88) * mm, v(13.75, -17.9) * mm, v(13.73, -17.96) * mm, v(13.7, -17.97) * mm]});
            skFitSpline(sketch, "E236", {"points": [v(13.7, -17.97) * mm, v(13.69, -17.98) * mm, v(13.67, -17.97) * mm, v(13.67, -17.97) * mm]});
            skFitSpline(sketch, "E237", {"points": [v(13.67, -17.97) * mm, v(13.66, -17.98) * mm, v(13.67, -18) * mm, v(13.67, -18) * mm]});
            skFitSpline(sketch, "E238", {"points": [v(13.67, -18) * mm, v(13.66, -18.01) * mm, v(13.65, -18) * mm, v(13.64, -18) * mm]});
            skFitSpline(sketch, "E239", {"points": [v(13.64, -18) * mm, v(13.61, -18.02) * mm, v(13.6, -18.05) * mm, v(13.58, -18.06) * mm]});
            skFitSpline(sketch, "E240", {"points": [v(13.58, -18.06) * mm, v(13.57, -18.07) * mm, v(13.56, -18.06) * mm, v(13.55, -18.06) * mm]});
            skFitSpline(sketch, "E241", {"points": [v(13.55, -18.06) * mm, v(13.53, -18.07) * mm, v(13.53, -18.09) * mm, v(13.52, -18.1) * mm]});
            skFitSpline(sketch, "E242", {"points": [v(13.52, -18.1) * mm, v(13.5, -18.1) * mm, v(13.5, -18.09) * mm, v(13.49, -18.1) * mm]});
            skFitSpline(sketch, "E243", {"points": [v(13.49, -18.1) * mm, v(13.47, -18.11) * mm, v(13.47, -18.14) * mm, v(13.46, -18.16) * mm]});
            skFitSpline(sketch, "E244", {"points": [v(13.46, -18.16) * mm, v(13.44, -18.17) * mm, v(13.41, -18.15) * mm, v(13.4, -18.16) * mm]});
            skFitSpline(sketch, "E245", {"points": [v(13.4, -18.16) * mm, v(13.38, -18.16) * mm, v(13.38, -18.18) * mm, v(13.37, -18.19) * mm]});
            skFitSpline(sketch, "E246", {"points": [v(13.37, -18.19) * mm, v(13.35, -18.2) * mm, v(13.32, -18.18) * mm, v(13.3, -18.19) * mm]});
            skFitSpline(sketch, "E247", {"points": [v(13.3, -18.19) * mm, v(13.28, -18.2) * mm, v(13.27, -18.23) * mm, v(13.25, -18.25) * mm]});
            skFitSpline(sketch, "E248", {"points": [v(13.25, -18.25) * mm, v(13.23, -18.25) * mm, v(13.2, -18.24) * mm, v(13.19, -18.25) * mm]});
            skFitSpline(sketch, "E249", {"points": [v(13.19, -18.25) * mm, v(13.17, -18.25) * mm, v(13.17, -18.27) * mm, v(13.16, -18.28) * mm]});
            skFitSpline(sketch, "E250", {"points": [v(13.16, -18.28) * mm, v(13.14, -18.28) * mm, v(13.11, -18.27) * mm, v(13.1, -18.28) * mm]});
            skFitSpline(sketch, "E251", {"points": [v(13.1, -18.28) * mm, v(13.08, -18.28) * mm, v(13.08, -18.3) * mm, v(13.07, -18.3) * mm]});
            skFitSpline(sketch, "E252", {"points": [v(13.07, -18.3) * mm, v(13.06, -18.3) * mm, v(13.04, -18.3) * mm, v(13.04, -18.3) * mm]});
            skFitSpline(sketch, "E253", {"points": [v(13.04, -18.3) * mm, v(13.03, -18.31) * mm, v(13.04, -18.33) * mm, v(13.04, -18.34) * mm]});
            skFitSpline(sketch, "E254", {"points": [v(13.04, -18.34) * mm, v(13.02, -18.35) * mm, v(13, -18.33) * mm, v(12.98, -18.34) * mm]});
            skFitSpline(sketch, "E255", {"points": [v(12.98, -18.34) * mm, v(12.84, -18.4) * mm, v(13.1, -18.32) * mm, v(12.89, -18.4) * mm]});
            skFitSpline(sketch, "E256", {"points": [v(12.89, -18.4) * mm, v(12.86, -18.4) * mm, v(12.82, -18.39) * mm, v(12.8, -18.4) * mm]});
            skFitSpline(sketch, "E257", {"points": [v(12.8, -18.4) * mm, v(12.78, -18.4) * mm, v(12.78, -18.42) * mm, v(12.77, -18.43) * mm]});
            skFitSpline(sketch, "E258", {"points": [v(12.77, -18.43) * mm, v(12.74, -18.44) * mm, v(12.7, -18.41) * mm, v(12.68, -18.43) * mm]});
            skFitSpline(sketch, "E259", {"points": [v(12.68, -18.43) * mm, v(12.66, -18.43) * mm, v(12.66, -18.45) * mm, v(12.65, -18.46) * mm]});
            skFitSpline(sketch, "E260", {"points": [v(12.65, -18.46) * mm, v(12.63, -18.46) * mm, v(12.6, -18.44) * mm, v(12.59, -18.46) * mm]});
            skFitSpline(sketch, "E261", {"points": [v(12.59, -18.46) * mm, v(12.58, -18.46) * mm, v(12.6, -18.48) * mm, v(12.59, -18.49) * mm]});
            skFitSpline(sketch, "E262", {"points": [v(12.59, -18.49) * mm, v(12.58, -18.5) * mm, v(12.49, -18.48) * mm, v(12.47, -18.49) * mm]});
            skFitSpline(sketch, "E263", {"points": [v(12.47, -18.49) * mm, v(12.25, -18.56) * mm, v(12.51, -18.48) * mm, v(12.38, -18.55) * mm]});
            skFitSpline(sketch, "E264", {"points": [v(12.38, -18.55) * mm, v(12.36, -18.56) * mm, v(12.27, -18.54) * mm, v(12.25, -18.55) * mm]});
            skFitSpline(sketch, "E265", {"points": [v(12.25, -18.55) * mm, v(12.24, -18.55) * mm, v(12.23, -18.57) * mm, v(12.22, -18.58) * mm]});
            skFitSpline(sketch, "E266", {"points": [v(12.22, -18.58) * mm, v(12.2, -18.58) * mm, v(12.16, -18.57) * mm, v(12.13, -18.58) * mm]});
            skFitSpline(sketch, "E267", {"points": [v(12.13, -18.58) * mm, v(12.13, -18.58) * mm, v(12.14, -18.6) * mm, v(12.13, -18.6) * mm]});
            skFitSpline(sketch, "E268", {"points": [v(12.13, -18.6) * mm, v(12.13, -18.61) * mm, v(12.03, -18.6) * mm, v(12.01, -18.6) * mm]});
            skFitSpline(sketch, "E269", {"points": [v(12.01, -18.6) * mm, v(12, -18.61) * mm, v(12, -18.63) * mm, v(11.98, -18.64) * mm]});
            skFitSpline(sketch, "E270", {"points": [v(11.98, -18.64) * mm, v(11.97, -18.64) * mm, v(11.85, -18.63) * mm, v(11.83, -18.64) * mm]});
            skFitSpline(sketch, "E271", {"points": [v(11.83, -18.64) * mm, v(11.82, -18.64) * mm, v(11.82, -18.66) * mm, v(11.8, -18.67) * mm]});
            skFitSpline(sketch, "E272", {"points": [v(11.8, -18.67) * mm, v(11.8, -18.67) * mm, v(11.78, -18.67) * mm, v(11.77, -18.67) * mm]});
            skFitSpline(sketch, "E273", {"points": [v(11.77, -18.67) * mm, v(11.76, -18.68) * mm, v(11.76, -18.69) * mm, v(11.74, -18.7) * mm]});
            skFitSpline(sketch, "E274", {"points": [v(11.74, -18.7) * mm, v(11.74, -18.7) * mm, v(11.64, -18.7) * mm, v(11.62, -18.7) * mm]});
            skFitSpline(sketch, "E275", {"points": [v(11.62, -18.7) * mm, v(11.51, -18.7) * mm, v(11.4, -18.7) * mm, v(11.3, -18.7) * mm]});
            skFitSpline(sketch, "E276", {"points": [v(11.3, -18.7) * mm, v(11.27, -18.7) * mm, v(11.19, -18.7) * mm, v(11.17, -18.7) * mm]});
            skFitSpline(sketch, "E277", {"points": [v(11.17, -18.7) * mm, v(11.16, -18.7) * mm, v(11.16, -18.72) * mm, v(11.14, -18.73) * mm]});
            skFitSpline(sketch, "E278", {"points": [v(11.14, -18.73) * mm, v(11.13, -18.73) * mm, v(10.98, -18.73) * mm, v(10.96, -18.73) * mm]});
            skFitSpline(sketch, "E279", {"points": [v(10.96, -18.73) * mm, v(10.95, -18.73) * mm, v(10.94, -18.72) * mm, v(10.93, -18.73) * mm]});
            skFitSpline(sketch, "E280", {"points": [v(10.93, -18.73) * mm, v(10.93, -18.73) * mm, v(10.94, -18.75) * mm, v(10.93, -18.76) * mm]});
            skFitSpline(sketch, "E281", {"points": [v(10.93, -18.76) * mm, v(10.92, -18.76) * mm, v(10.77, -18.76) * mm, v(10.75, -18.76) * mm]});
            skFitSpline(sketch, "E282", {"points": [v(10.75, -18.76) * mm, v(10.74, -18.76) * mm, v(10.73, -18.75) * mm, v(10.72, -18.76) * mm]});
            skFitSpline(sketch, "E283", {"points": [v(10.72, -18.76) * mm, v(10.72, -18.76) * mm, v(10.73, -18.78) * mm, v(10.72, -18.79) * mm]});
            skFitSpline(sketch, "E284", {"points": [v(10.72, -18.79) * mm, v(10.72, -18.79) * mm, v(10.58, -18.79) * mm, v(10.57, -18.79) * mm]});
            skFitSpline(sketch, "E285", {"points": [v(10.57, -18.79) * mm, v(10.45, -18.79) * mm, v(10.33, -18.79) * mm, v(10.21, -18.79) * mm]});
            skFitSpline(sketch, "E286", {"points": [v(10.21, -18.79) * mm, v(10.08, -18.79) * mm, v(9.95, -18.79) * mm, v(9.82, -18.79) * mm]});
            skFitSpline(sketch, "E287", {"points": [v(9.82, -18.79) * mm, v(9.8, -18.79) * mm, v(9.65, -18.8) * mm, v(9.64, -18.79) * mm]});
            skFitSpline(sketch, "E288", {"points": [v(9.64, -18.79) * mm, v(9.63, -18.78) * mm, v(9.62, -18.76) * mm, v(9.61, -18.76) * mm]});
            skFitSpline(sketch, "E289", {"points": [v(9.61, -18.76) * mm, v(9.6, -18.75) * mm, v(9.57, -18.77) * mm, v(9.55, -18.76) * mm]});
            skFitSpline(sketch, "E290", {"points": [v(9.55, -18.76) * mm, v(9.54, -18.75) * mm, v(9.53, -18.73) * mm, v(9.52, -18.73) * mm]});
            skFitSpline(sketch, "E291", {"points": [v(9.52, -18.73) * mm, v(9.51, -18.72) * mm, v(9.5, -18.73) * mm, v(9.5, -18.73) * mm]});
            skFitSpline(sketch, "E292", {"points": [v(9.5, -18.73) * mm, v(9.48, -18.72) * mm, v(9.47, -18.7) * mm, v(9.46, -18.7) * mm]});
            skFitSpline(sketch, "E293", {"points": [v(9.46, -18.7) * mm, v(9.44, -18.68) * mm, v(9.42, -18.68) * mm, v(9.4, -18.67) * mm]});
            skFitSpline(sketch, "E294", {"points": [v(9.4, -18.67) * mm, v(9.4, -18.66) * mm, v(9.4, -18.64) * mm, v(9.4, -18.64) * mm]});
            skFitSpline(sketch, "E295", {"points": [v(9.4, -18.64) * mm, v(9.4, -18.63) * mm, v(9.38, -18.64) * mm, v(9.37, -18.64) * mm]});
            skFitSpline(sketch, "E296", {"points": [v(9.37, -18.64) * mm, v(9.36, -18.63) * mm, v(9.37, -18.62) * mm, v(9.37, -18.6) * mm]});
            skFitSpline(sketch, "E297", {"points": [v(9.37, -18.6) * mm, v(9.36, -18.58) * mm, v(9.35, -18.57) * mm, v(9.34, -18.55) * mm]});
            skFitSpline(sketch, "E298", {"points": [v(9.34, -18.55) * mm, v(9.33, -18.53) * mm, v(9.34, -18.45) * mm, v(9.34, -18.43) * mm]});
            skFitSpline(sketch, "E299", {"points": [v(9.34, -18.43) * mm, v(9.34, -18.42) * mm, v(9.34, -18.4) * mm, v(9.34, -18.4) * mm]});
            skFitSpline(sketch, "E300", {"points": [v(9.34, -18.4) * mm, v(9.34, -18.39) * mm, v(9.33, -18.37) * mm, v(9.34, -18.37) * mm]});
            skFitSpline(sketch, "E301", {"points": [v(9.34, -18.37) * mm, v(9.39, -18.32) * mm, v(9.44, -18.29) * mm, v(9.5, -18.25) * mm]});
            skSolve(sketch);
        }
        {
            var Q0;
            Q0=qCreatedBy(makeId("Top.planeOp"),FACE);
            var sketch = newSketch(context, id + "F1", { "sketchPlane" : qUnion([Q0])});
            skFitSpline(sketch, "E302", {"points": [v(-4.69, -0.97) * mm, v(-3.59, -0.63) * mm, v(-3.16, 0.04) * mm, v(0.76, 1.18) * mm, v(3.94, 1.83) * mm, v(4.09, 2.62) * mm, v(0.36, 2.79) * mm, v(-2.7, 2.24) * mm, v(-3.3, 1.94) * mm, v(-4.52, 0.33) * mm, v(-4.69, -0.97) * mm]});
            skFitSpline(sketch, "E303", {"points": [v(13.04, 7.32) * mm, v(9.43, 5.38) * mm, v(8.84, 4.98) * mm, v(8.98, 4.64) * mm]});
            skFitSpline(sketch, "E304", {"points": [v(8.98, 4.64) * mm, v(9.29, 3.85) * mm, v(10, 3.94) * mm, v(11.83, 4.9) * mm]});
            skFitSpline(sketch, "E305", {"points": [v(11.83, 4.9) * mm, v(14.2, 6.17) * mm, v(15.05, 6.17) * mm, v(15.98, 4.98) * mm]});
            skFitSpline(sketch, "E306", {"points": [v(15.98, 4.98) * mm, v(16.51, 4.3) * mm, v(16.77, 4.14) * mm, v(17, 4.36) * mm]});
            skFitSpline(sketch, "E307", {"points": [v(17, 4.36) * mm, v(17.36, 4.73) * mm, v(16.77, 6.11) * mm, v(15.84, 7.04) * mm]});
            skFitSpline(sketch, "E308", {"points": [v(15.84, 7.04) * mm, v(15.27, 7.6) * mm, v(13.83, 7.75) * mm, v(13.04, 7.32) * mm]});
            skSolve(sketch);
        }
        {
            var Q0;
            Q0 = qSketchRegion(id + "F1", true);
            extrude(context, id + "F2", {"entities" : qUnion([Q0]), "depth" : 2.54 * mm, "offsetDistance" : 25.4 * mm});
        }
        {
            var Q0;
            Q0 = qSketchRegion(id + "F0", true);
            extrude(context, id + "F3", {"entities" : qUnion([Q0]), "depth" : 2.54 * mm, "offsetDistance" : 25.4 * mm});
        }
        {
            var Q0;
            Q0=qCreatedBy(makeId("Top.planeOp"),FACE);
            var sketch = newSketch(context, id + "F4", { "sketchPlane" : qUnion([Q0])});
            skLineSegment(sketch, "E309", {"start": v(16.8, 11.07) * mm, "end": v(15.81, 13.05) * mm});
            skLineSegment(sketch, "E310", {"start": v(15.81, 13.05) * mm, "end": v(17.5, 13.05) * mm});
            skLineSegment(sketch, "E311", {"start": v(17.5, 13.05) * mm, "end": v(16.8, 11.07) * mm});
            skFitSpline(sketch, "E312", {"points": [v(-3.35, 24.9) * mm, v(-5.58, 24.59) * mm, v(-8.71, 23.66) * mm, v(-10.43, 22.78) * mm]});
            skFitSpline(sketch, "E313", {"points": [v(-10.43, 22.78) * mm, v(-12.83, 21.57) * mm, v(-16, 18.24) * mm, v(-17.86, 14.96) * mm]});
            skFitSpline(sketch, "E314", {"points": [v(-17.86, 14.96) * mm, v(-19.21, 12.62) * mm, v(-20.62, 8.56) * mm, v(-20.8, 6.55) * mm]});
            skFitSpline(sketch, "E315", {"points": [v(-20.8, 6.55) * mm, v(-20.93, 4.86) * mm, v(-20.88, 4.58) * mm, v(-20.2, 3.5) * mm]});
            skFitSpline(sketch, "E316", {"points": [v(-20.2, 3.5) * mm, v(-19.8, 2.86) * mm, v(-19.47, 2.1) * mm, v(-19.47, 1.81) * mm]});
            skFitSpline(sketch, "E317", {"points": [v(-19.47, 1.81) * mm, v(-19.47, -0.78) * mm, v(-15.85, -9.56) * mm, v(-13.23, -13.34) * mm]});
            skFitSpline(sketch, "E318", {"points": [v(-13.23, -13.34) * mm, v(-10.6, -17.18) * mm, v(-8.83, -18.53) * mm, v(-2.67, -21.55) * mm]});
            skFitSpline(sketch, "E319", {"points": [v(-2.67, -21.55) * mm, v(3.45, -24.52) * mm, v(5.09, -25.05) * mm, v(8.3, -25.05) * mm]});
            skFitSpline(sketch, "E320", {"points": [v(8.3, -25.05) * mm, v(10.34, -25.05) * mm, v(10.76, -24.94) * mm, v(12.85, -23.93) * mm]});
            skFitSpline(sketch, "E321", {"points": [v(12.85, -23.93) * mm, v(15.28, -22.77) * mm, v(15.87, -22.18) * mm, v(17.42, -19.4) * mm]});
            skFitSpline(sketch, "E322", {"points": [v(17.42, -19.4) * mm, v(18.66, -17.18) * mm, v(19.65, -14.27) * mm, v(20.3, -10.8) * mm]});
            skFitSpline(sketch, "E323", {"points": [v(20.3, -10.8) * mm, v(21.03, -7.05) * mm, v(21.03, -4.82) * mm, v(20.33, -1.1) * mm]});
            skFitSpline(sketch, "E324", {"points": [v(20.33, -1.1) * mm, v(20.02, 0.54) * mm, v(19.82, 2.04) * mm, v(19.9, 2.26) * mm]});
            skFitSpline(sketch, "E325", {"points": [v(19.9, 2.26) * mm, v(19.99, 2.46) * mm, v(19.85, 2.83) * mm, v(19.62, 3.06) * mm]});
            skFitSpline(sketch, "E326", {"points": [v(19.62, 3.06) * mm, v(19.4, 3.3) * mm, v(19.2, 3.82) * mm, v(19.2, 4.18) * mm]});
            skFitSpline(sketch, "E327", {"points": [v(19.2, 4.18) * mm, v(19.2, 5.2) * mm, v(17.96, 8.78) * mm, v(16.8, 11.07) * mm]});
            skFitSpline(sketch, "E328", {"points": [v(17.5, 13.05) * mm, v(19.11, 13.05) * mm, v(19.2, 13.07) * mm, v(19.2, 13.72) * mm]});
            skFitSpline(sketch, "E329", {"points": [v(19.2, 13.72) * mm, v(19.2, 14.43) * mm, v(17.76, 15.78) * mm, v(16.3, 16.46) * mm]});
            skFitSpline(sketch, "E330", {"points": [v(16.3, 16.46) * mm, v(15.76, 16.69) * mm, v(15.56, 16.97) * mm, v(15.67, 17.28) * mm]});
            skFitSpline(sketch, "E331", {"points": [v(15.67, 17.28) * mm, v(15.9, 17.98) * mm, v(15.36, 19.17) * mm, v(14.6, 19.68) * mm]});
            skFitSpline(sketch, "E332", {"points": [v(14.6, 19.68) * mm, v(14.2, 19.93) * mm, v(12.26, 20.78) * mm, v(10.28, 21.54) * mm]});
            skFitSpline(sketch, "E333", {"points": [v(10.28, 21.54) * mm, v(1.48, 25.01) * mm, v(0.1, 25.35) * mm, v(-3.35, 24.9) * mm]});
            skFitSpline(sketch, "E334", {"points": [v(3.82, 23.35) * mm, v(8.1, 21.8) * mm, v(13.58, 19.6) * mm, v(14.29, 19.11) * mm]});
            skFitSpline(sketch, "E335", {"points": [v(14.29, 19.11) * mm, v(14.97, 18.7) * mm, v(15.08, 18.32) * mm, v(14.97, 17.08) * mm]});
            skFitSpline(sketch, "E336", {"points": [v(14.97, 17.08) * mm, v(14.94, 16.63) * mm, v(15.2, 16.32) * mm, v(15.87, 15.98) * mm]});
            skFitSpline(sketch, "E337", {"points": [v(15.87, 15.98) * mm, v(17.11, 15.36) * mm, v(18.63, 14.17) * mm, v(18.63, 13.86) * mm]});
            skFitSpline(sketch, "E338", {"points": [v(18.63, 13.86) * mm, v(18.63, 13.72) * mm, v(17.93, 13.61) * mm, v(17.08, 13.61) * mm]});
            skFitSpline(sketch, "E339", {"points": [v(17.08, 13.61) * mm, v(16.01, 13.61) * mm, v(15.47, 13.5) * mm, v(15.36, 13.22) * mm]});
            skFitSpline(sketch, "E340", {"points": [v(15.36, 13.22) * mm, v(15.28, 12.99) * mm, v(15.62, 12.06) * mm, v(16.07, 11.1) * mm]});
            skFitSpline(sketch, "E341", {"points": [v(16.07, 11.1) * mm, v(17.9, 7.51) * mm, v(18.27, 6.24) * mm, v(19.62, -0.78) * mm]});
            skFitSpline(sketch, "E342", {"points": [v(19.62, -0.78) * mm, v(20.47, -5.1) * mm, v(20.5, -6.68) * mm, v(19.74, -10.52) * mm]});
            skFitSpline(sketch, "E343", {"points": [v(19.74, -10.52) * mm, v(19.06, -14.05) * mm, v(18.1, -16.9) * mm, v(16.77, -19.3) * mm]});
            skFitSpline(sketch, "E344", {"points": [v(16.77, -19.3) * mm, v(15.42, -21.72) * mm, v(14.68, -22.43) * mm, v(12.28, -23.53) * mm]});
            skFitSpline(sketch, "E345", {"points": [v(12.28, -23.53) * mm, v(10.56, -24.32) * mm, v(9.89, -24.49) * mm, v(8.28, -24.49) * mm]});
            skFitSpline(sketch, "E346", {"points": [v(8.28, -24.49) * mm, v(5.4, -24.49) * mm, v(3.6, -23.9) * mm, v(-2.36, -21) * mm]});
            skFitSpline(sketch, "E347", {"points": [v(-2.36, -21) * mm, v(-8.51, -18) * mm, v(-10.12, -16.76) * mm, v(-12.66, -13.09) * mm]});
            skFitSpline(sketch, "E348", {"points": [v(-12.66, -13.09) * mm, v(-15.29, -9.28) * mm, v(-18.9, -0.5) * mm, v(-18.9, 2.1) * mm]});
            skFitSpline(sketch, "E349", {"points": [v(-18.9, 2.1) * mm, v(-18.9, 2.38) * mm, v(-19.24, 3.14) * mm, v(-19.63, 3.79) * mm]});
            skFitSpline(sketch, "E350", {"points": [v(-19.63, 3.79) * mm, v(-20.28, 4.83) * mm, v(-20.37, 5.14) * mm, v(-20.2, 6.61) * mm]});
            skFitSpline(sketch, "E351", {"points": [v(-20.2, 6.61) * mm, v(-20.03, 8.39) * mm, v(-18.53, 12.54) * mm, v(-17.32, 14.68) * mm]});
            skFitSpline(sketch, "E352", {"points": [v(-17.32, 14.68) * mm, v(-15.46, 17.93) * mm, v(-12.44, 21.09) * mm, v(-10.01, 22.3) * mm]});
            skFitSpline(sketch, "E353", {"points": [v(-10.01, 22.3) * mm, v(-7.27, 23.66) * mm, v(-2.45, 24.7) * mm, v(0, 24.4) * mm]});
            skFitSpline(sketch, "E354", {"points": [v(0, 24.4) * mm, v(0.71, 24.33) * mm, v(2.44, 23.85) * mm, v(3.82, 23.35) * mm]});
            skSolve(sketch);
        }
        {
            var Q0;
            Q0 = qSketchRegion(id + "F4", true);
            extrude(context, id + "F5", {"entities" : qUnion([Q0]), "operationType" : NewBodyOperationType.ADD, "depth" : 3.8 * mm, "offsetDistance" : 25.4 * mm});
        }
        {
            var Q0;
            Q0=qCreatedBy(makeId("Top.planeOp"),FACE);
            var sketch = newSketch(context, id + "F6", { "sketchPlane" : qUnion([Q0])});
            skFitSpline(sketch, "E355", {"points": [v(6.4, -16.66) * mm, v(8.29, -16.79) * mm, v(10.7, -16.46) * mm, v(13.14, -15.68) * mm, v(14.7, -14.89) * mm, v(14.57, -14.63) * mm, v(14.52, -14.22) * mm, v(14.77, -14.07) * mm, v(15.42, -14.72) * mm, v(15.57, -15.36) * mm, v(14.78, -15.6) * mm, v(13.2, -16.39) * mm, v(11.2, -17.07) * mm, v(9.08, -17.3) * mm, v(7.27, -17.47) * mm, v(6.11, -17.44) * mm, v(5.78, -17.71) * mm, v(5.46, -17.06) * mm, v(5.99, -16.28) * mm, v(6.4, -16.66) * mm]});
            skFitSpline(sketch, "E356", {"points": [v(9.5, -18.17) * mm, v(9.34, -18.3) * mm, v(9.36, -18.6) * mm, v(9.66, -18.72) * mm, v(11.65, -18.67) * mm, v(13.43, -18.17) * mm, v(13.94, -17.58) * mm, v(13.68, -17.23) * mm, v(12.22, -17.68) * mm, v(10.94, -17.98) * mm, v(9.5, -18.17) * mm]});
            skSolve(sketch);
        }
        {
            var Q0;
            Q0 = qSketchRegion(id + "F6", true);
            extrude(context, id + "F7", {"entities" : qUnion([Q0]), "depth" : 2.54 * mm, "offsetDistance" : 25.4 * mm});
        }
        {
            var Q0;
            Q0=qCreatedBy(makeId("Top.planeOp"),FACE);
            var sketch = newSketch(context, id + "F8", { "sketchPlane" : qUnion([Q0])});
            skEllipse(sketch, "E357", {"center": v(1.58, -3.93) * mm, "majorRadius": 4.44 * mm, "minorRadius": 2.32 * mm, "majorAxis": v(0.99, 0.17)});
            skEllipticalArc(sketch, "E358", {});
            skEllipse(sketch, "E359", {"center": v(13.8, -0.93) * mm, "majorRadius": 3.81 * mm, "minorRadius": 2.24 * mm, "majorAxis": v(0.97, 0.25)});
            skEllipticalArc(sketch, "E360", {});
            skArc(sketch, "E361", {"start": v(0.4, -2.43) * mm, "mid": v(-0.3, -4.26) * mm, "end": v(1, -5.74) * mm});
            skCircle(sketch, "E362", {"center": v(1.58, -3.93) * mm, "radius": 1.61 * mm});
            skCircle(sketch, "E363", {"center": v(1.58, -3.93) * mm, "radius": 0.57 * mm});
            skArc(sketch, "E364.trimOffspring", {"start": v(2.76, -5.43) * mm, "mid": v(3.46, -3.6) * mm, "end": v(2.17, -2.12) * mm});
            skEllipticalArc(sketch, "E365.trimOffspring", {});
            skArc(sketch, "E366", {"start": v(12.37, 0.39) * mm, "mid": v(11.92, -1.43) * mm, "end": v(13.22, -2.78) * mm});
            skCircle(sketch, "E367", {"center": v(13.8, -0.93) * mm, "radius": 1.7 * mm});
            skEllipticalArc(sketch, "E368.trimOffspring", {});
            skArc(sketch, "E369.trimOffspring", {"start": v(15.24, -2.24) * mm, "mid": v(15.68, -0.42) * mm, "end": v(14.39, 0.93) * mm});
            skCircle(sketch, "E370", {"center": v(13.8, -0.93) * mm, "radius": 0.67 * mm});
            const initialGuessF8  = {"E358": [0.0015835562953725457, -0.0039305901154875755, -0.9846563677001892, -0.17450454878733096, 0.0035355052423248386, 0.0017385843149818091, 4.968557087860097, 1.3146282193194896], "E360": [0.013804391957819462, -0.0009273597970604897, -0.9657003793828, -0.2596589633729526, 0.003175, 0.0017385843149818091, 5.048669190645864, 1.2345161165337224], "E365.trimOffspring": [0.0015835562953725457, -0.0039305901154875755, -0.9846563677001892, -0.17450454878733096, 0.0035355052423248386, 0.0017385843149818091, 1.8269644342703035, 4.456220872909282], "E368.trimOffspring": [0.013804391957819462, -0.0009273597970604897, -0.9657003793828, -0.2596589633729526, 0.003175, 0.0017385843149818091, 1.9070765370560725, 4.376108770123515]};
            skSetInitialGuess(sketch, initialGuessF8);
            skSolve(sketch);
        }
        {
            var Q0;
            Q0 = qSketchRegion(id + "F8", true);
            extrude(context, id + "F9", {"entities" : qUnion([Q0]), "operationType" : NewBodyOperationType.ADD, "depth" : 2.54 * mm, "offsetDistance" : 25.4 * mm});
        }
        {
            var Q0;
            Q0=qCreatedBy(makeId("Top.planeOp"),FACE);
            var sketch = newSketch(context, id + "F10", { "sketchPlane" : qUnion([Q0])});
            skCircle(sketch, "E371", {"center": v(1.57, -3.92) * mm, "radius": 0.66 * mm});
            skCircle(sketch, "E372", {"center": v(13.83, -0.97) * mm, "radius": 0.78 * mm});
            skSolve(sketch);
        }
        {
            var Q0;
            Q0 = qSketchRegion(id + "F10", true);
            extrude(context, id + "F11", {"entities" : qUnion([Q0]), "depth" : 2.54 * mm, "offsetDistance" : 25.4 * mm});
        }
        {
            var Q0;
            Q0=qCreatedBy(makeId("Top.planeOp"),FACE);
            var sketch = newSketch(context, id + "F12", { "sketchPlane" : qUnion([Q0])});
            skLineSegment(sketch, "E373", {"start": v(-17.62, -2.47) * mm, "end": v(0.52, 2.9) * mm});
            skLineSegment(sketch, "E374", {"start": v(17.29, 7.86) * mm, "end": v(18.02, 5.37) * mm});
            skLineSegment(sketch, "E375", {"start": v(18.02, 5.37) * mm, "end": v(8.18, 2.46) * mm});
            skLineSegment(sketch, "E376", {"start": v(-16.9, -4.95) * mm, "end": v(-17.62, -2.47) * mm});
            skLineSegment(sketch, "E377", {"start": v(14.4, -22.52) * mm, "end": v(10.18, -5.6) * mm});
            skLineSegment(sketch, "E378", {"start": v(2.89, 23.69) * mm, "end": v(-1.6, 24.62) * mm});
            skLineSegment(sketch, "E379", {"start": v(-1.6, 24.62) * mm, "end": v(-5.62, 23.69) * mm});
            skLineSegment(sketch, "E380", {"start": v(-5.62, 23.69) * mm, "end": v(0.52, 2.9) * mm});
            skLineSegment(sketch, "E381", {"start": v(8.75, -24.92) * mm, "end": v(11.96, -23.98) * mm});
            skLineSegment(sketch, "E382", {"start": v(11.96, -23.98) * mm, "end": v(14.4, -22.52) * mm});
            skLineSegment(sketch, "E383", {"start": v(1.72, -1.14) * mm, "end": v(-2.18, -1.93) * mm});
            skLineSegment(sketch, "E384", {"start": v(-2.18, -1.93) * mm, "end": v(-4.19, -3.26) * mm});
            skLineSegment(sketch, "E385", {"start": v(-4.19, -3.26) * mm, "end": v(-3.46, -6.61) * mm});
            skLineSegment(sketch, "E386", {"start": v(-3.46, -6.61) * mm, "end": v(-1.96, -8.23) * mm});
            skLineSegment(sketch, "E387", {"start": v(-1.96, -8.23) * mm, "end": v(0.89, -8) * mm});
            skLineSegment(sketch, "E388", {"start": v(0.89, -8) * mm, "end": v(3.55, -7.32) * mm});
            skLineSegment(sketch, "E389", {"start": v(18.52, -3.44) * mm, "end": v(19.17, -1.73) * mm});
            skLineSegment(sketch, "E390", {"start": v(19.17, -1.73) * mm, "end": v(18.82, 1.02) * mm});
            skLineSegment(sketch, "E391", {"start": v(18.82, 1.02) * mm, "end": v(17.8, 2.4) * mm});
            skLineSegment(sketch, "E392", {"start": v(17.8, 2.4) * mm, "end": v(16.02, 2.4) * mm});
            skLineSegment(sketch, "E393", {"start": v(16.02, 2.4) * mm, "end": v(8.65, 0.57) * mm});
            skLineSegment(sketch, "E394.trimOffspring", {"start": v(3.55, -7.32) * mm, "end": v(8.75, -24.92) * mm});
            skLineSegment(sketch, "E395.trimOffspring", {"start": v(8.65, 0.57) * mm, "end": v(8.18, 2.46) * mm});
            skLineSegment(sketch, "E396.trimOffspring", {"start": v(10.18, -5.6) * mm, "end": v(18.52, -3.44) * mm});
            skLineSegment(sketch, "E397.trimOffspring", {"start": v(7.55, 4.98) * mm, "end": v(17.29, 7.86) * mm});
            skLineSegment(sketch, "E398.trimOffspring", {"start": v(1.26, 0.41) * mm, "end": v(-16.9, -4.95) * mm});
            skLineSegment(sketch, "E399.trimOffspring", {"start": v(1.26, 0.41) * mm, "end": v(1.72, -1.14) * mm});
            skLineSegment(sketch, "E400.trimOffspring", {"start": v(7.55, 4.98) * mm, "end": v(2.89, 23.69) * mm});
            skSolve(sketch);
        }
        {
            var Q0;
            Q0 = qSketchRegion(id + "F12", true);
            extrude(context, id + "F13", {"entities" : qUnion([Q0]), "depth" : 0.64 * mm, "offsetDistance" : 25.4 * mm});
        }
    });
